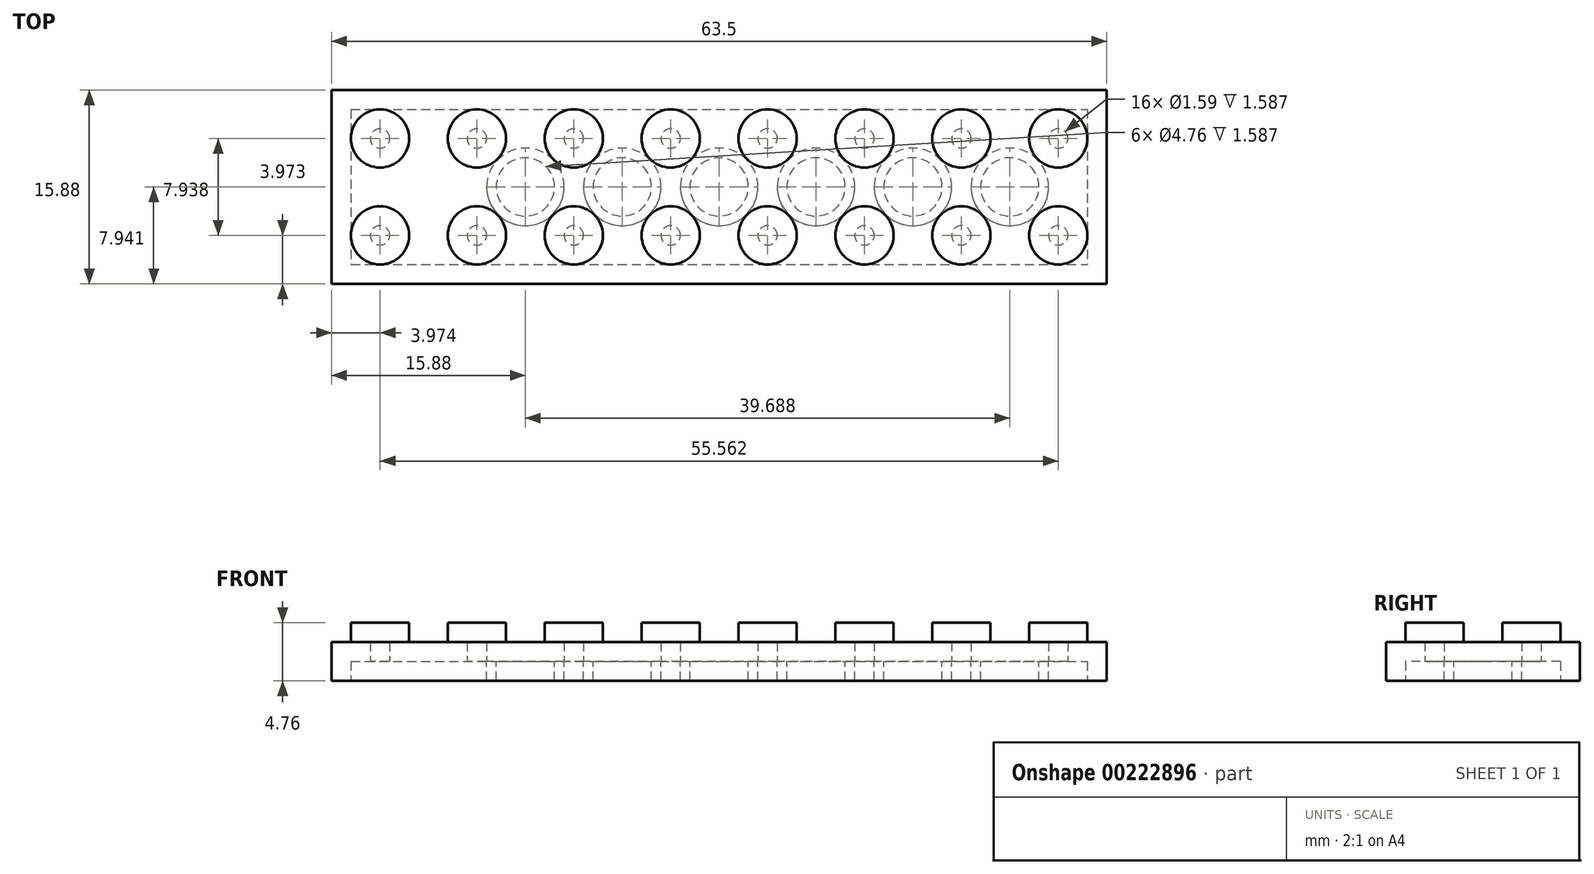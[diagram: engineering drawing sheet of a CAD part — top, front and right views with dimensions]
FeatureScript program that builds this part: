
annotation { "Feature Type Name" : "Feature", "Feature Type Description" : "" }
export const myFeature = defineFeature(function(context is Context, id is Id, definition is map)
    precondition{}
    {
        {
            var Q0;
            Q0=qCreatedBy(makeId("Top.planeOp"),FACE);
            var sketch = newSketch(context, id + "F0", { "sketchPlane" : qUnion([Q0])});
            skLineSegment(sketch, "E0.bottom", {"start": v(-15.88, 3.97) * mm, "end": v(47.62, 3.97) * mm});
            skLineSegment(sketch, "E0.top", {"start": v(-15.88, -11.9) * mm, "end": v(47.62, -11.9) * mm});
            skLineSegment(sketch, "E0.left", {"start": v(-15.88, 3.97) * mm, "end": v(-15.88, -11.9) * mm});
            skLineSegment(sketch, "E0.right", {"start": v(47.62, 3.97) * mm, "end": v(47.62, -11.9) * mm});
            skCircle(sketch, "E1", {"center": v(-11.9, 0) * mm, "radius": 2.38 * mm});
            skCircle(sketch, "E2.0.1.0", {"center": v(-11.9, -7.94) * mm, "radius": 2.38 * mm});
            skCircle(sketch, "E2.1.0.0", {"center": v(-3.97, 0) * mm, "radius": 2.38 * mm});
            skCircle(sketch, "E2.1.1.0", {"center": v(-3.97, -7.94) * mm, "radius": 2.38 * mm});
            skCircle(sketch, "E2.2.0.0", {"center": v(3.97, 0) * mm, "radius": 2.38 * mm});
            skCircle(sketch, "E2.2.1.0", {"center": v(3.97, -7.94) * mm, "radius": 2.38 * mm});
            skCircle(sketch, "E2.3.0.0", {"center": v(11.9, 0) * mm, "radius": 2.38 * mm});
            skCircle(sketch, "E2.3.1.0", {"center": v(11.9, -7.94) * mm, "radius": 2.38 * mm});
            skLineSegment(sketch, "E2.direction1", {"start": v(-11.9, 0) * mm, "end": v(-3.97, 0) * mm, "construction": true});
            skLineSegment(sketch, "E2.direction2", {"start": v(-11.9, 0) * mm, "end": v(-11.9, -7.94) * mm, "construction": true});
            skCircle(sketch, "E3.0.4.0", {"center": v(19.84, 0) * mm, "radius": 2.38 * mm});
            skCircle(sketch, "E3.0.4.1", {"center": v(19.84, -7.94) * mm, "radius": 2.38 * mm});
            skCircle(sketch, "E3.0.5.0", {"center": v(27.78, 0) * mm, "radius": 2.38 * mm});
            skCircle(sketch, "E3.0.5.1", {"center": v(27.78, -7.94) * mm, "radius": 2.38 * mm});
            skCircle(sketch, "E4.0.6.0", {"center": v(35.72, 0) * mm, "radius": 2.38 * mm});
            skCircle(sketch, "E4.0.6.1", {"center": v(35.72, -7.94) * mm, "radius": 2.38 * mm});
            skCircle(sketch, "E4.0.7.0", {"center": v(43.66, 0) * mm, "radius": 2.38 * mm});
            skCircle(sketch, "E4.0.7.1", {"center": v(43.66, -7.94) * mm, "radius": 2.38 * mm});
            skSolve(sketch);
        }
        {
            var Q0;
            Q0=makeQuery(id+"F0.imprint","IMPRINT",FACE,{"disambiguationData":[TD([[makeQuery(id+"F0.imprint","IMPRINT",EDGE,{"derivedFrom":sQuery(id+"F0.wireOp",EDGE,"E0.bottom")}),-1.0]])]});
            extrude(context, id + "F1", {"entities" : qUnion([Q0]), "depth" : 3.17 * mm});
        }
        {
            var Q0;
            Q0=makeQuery(id+"F0.imprint","IMPRINT",FACE,{"disambiguationData":[TD([[makeQuery(id+"F0.imprint","IMPRINT",EDGE,{"derivedFrom":sQuery(id+"F0.wireOp",EDGE,"E1")}),1.0]])]});
            var Q1;
            Q1=makeQuery(id+"F0.imprint","IMPRINT",FACE,{"disambiguationData":[TD([[makeQuery(id+"F0.imprint","IMPRINT",EDGE,{"derivedFrom":sQuery(id+"F0.wireOp",EDGE,"E2.0.1.0")}),1.0]])]});
            var Q2;
            Q2=makeQuery(id+"F0.imprint","IMPRINT",FACE,{"disambiguationData":[TD([[makeQuery(id+"F0.imprint","IMPRINT",EDGE,{"derivedFrom":sQuery(id+"F0.wireOp",EDGE,"E2.1.1.0")}),1.0]])]});
            var Q3;
            Q3=makeQuery(id+"F0.imprint","IMPRINT",FACE,{"disambiguationData":[TD([[makeQuery(id+"F0.imprint","IMPRINT",EDGE,{"derivedFrom":sQuery(id+"F0.wireOp",EDGE,"E2.1.0.0")}),1.0]])]});
            var Q4;
            Q4=makeQuery(id+"F0.imprint","IMPRINT",FACE,{"disambiguationData":[TD([[makeQuery(id+"F0.imprint","IMPRINT",EDGE,{"derivedFrom":sQuery(id+"F0.wireOp",EDGE,"E2.2.0.0")}),1.0]])]});
            var Q5;
            Q5=makeQuery(id+"F0.imprint","IMPRINT",FACE,{"disambiguationData":[TD([[makeQuery(id+"F0.imprint","IMPRINT",EDGE,{"derivedFrom":sQuery(id+"F0.wireOp",EDGE,"E2.2.1.0")}),1.0]])]});
            var Q6;
            Q6=makeQuery(id+"F0.imprint","IMPRINT",FACE,{"disambiguationData":[TD([[makeQuery(id+"F0.imprint","IMPRINT",EDGE,{"derivedFrom":sQuery(id+"F0.wireOp",EDGE,"E2.3.1.0")}),1.0]])]});
            var Q7;
            Q7=makeQuery(id+"F0.imprint","IMPRINT",FACE,{"disambiguationData":[TD([[makeQuery(id+"F0.imprint","IMPRINT",EDGE,{"derivedFrom":sQuery(id+"F0.wireOp",EDGE,"E2.3.0.0")}),1.0]])]});
            var Q8;
            Q8=makeQuery(id+"F0.imprint","IMPRINT",FACE,{"disambiguationData":[TD([[makeQuery(id+"F0.imprint","IMPRINT",EDGE,{"derivedFrom":sQuery(id+"F0.wireOp",EDGE,"E3.0.4.0")}),1.0]])]});
            var Q9;
            Q9=makeQuery(id+"F0.imprint","IMPRINT",FACE,{"disambiguationData":[TD([[makeQuery(id+"F0.imprint","IMPRINT",EDGE,{"derivedFrom":sQuery(id+"F0.wireOp",EDGE,"E3.0.5.0")}),1.0]])]});
            var Q10;
            Q10=makeQuery(id+"F0.imprint","IMPRINT",FACE,{"disambiguationData":[TD([[makeQuery(id+"F0.imprint","IMPRINT",EDGE,{"derivedFrom":sQuery(id+"F0.wireOp",EDGE,"E3.0.5.1")}),1.0]])]});
            var Q11;
            Q11=makeQuery(id+"F0.imprint","IMPRINT",FACE,{"disambiguationData":[TD([[makeQuery(id+"F0.imprint","IMPRINT",EDGE,{"derivedFrom":sQuery(id+"F0.wireOp",EDGE,"E3.0.4.1")}),1.0]])]});
            var Q12;
            Q12=makeQuery(id+"F0.imprint","IMPRINT",FACE,{"disambiguationData":[TD([[makeQuery(id+"F0.imprint","IMPRINT",EDGE,{"derivedFrom":sQuery(id+"F0.wireOp",EDGE,"E4.0.6.0")}),1.0]])]});
            var Q13;
            Q13=makeQuery(id+"F0.imprint","IMPRINT",FACE,{"disambiguationData":[TD([[makeQuery(id+"F0.imprint","IMPRINT",EDGE,{"derivedFrom":sQuery(id+"F0.wireOp",EDGE,"E4.0.7.0")}),1.0]])]});
            var Q14;
            Q14=makeQuery(id+"F0.imprint","IMPRINT",FACE,{"disambiguationData":[TD([[makeQuery(id+"F0.imprint","IMPRINT",EDGE,{"derivedFrom":sQuery(id+"F0.wireOp",EDGE,"E4.0.7.1")}),1.0]])]});
            var Q15;
            Q15=makeQuery(id+"F0.imprint","IMPRINT",FACE,{"disambiguationData":[TD([[makeQuery(id+"F0.imprint","IMPRINT",EDGE,{"derivedFrom":sQuery(id+"F0.wireOp",EDGE,"E4.0.6.1")}),1.0]])]});
            extrude(context, id + "F2", {"entities" : qUnion([Q0, Q1, Q2, Q3, Q4, Q5, Q6, Q7, Q8, Q9, Q10, Q11, Q12, Q13, Q14, Q15]), "operationType" : NewBodyOperationType.ADD, "depth" : 4.76 * mm});
        }
        {
            var Q0;
            {var subQ0=sQuery(id+"F0.wireOp",EDGE,"8b71ed98-f0e1-4300-85cb-82ad82c44b3e0.MirrorC");var subQ1=sQuery(id+"F0.wireOp",EDGE,"E1");Q0=makeQuery(id+"F2.boolean.opBoolean","MERGE",FACE,{"derivedFrom":[makeQuery(id+"F1.opExtrude","CAP_FACE",FACE,{"disambiguationData":[OSD([sQuery(id+"F0.wireOp",EDGE,"E0.bottom"),sQuery(id+"F0.wireOp",EDGE,"E0.top"),sQuery(id+"F0.wireOp",EDGE,"E0.left"),sQuery(id+"F0.wireOp",EDGE,"E0.right"),subQ1,subQ0])],"isStart":true}),makeQuery(id+"F2.opExtrude","CAP_FACE",FACE,{"disambiguationData":[OSD([subQ1])],"isStart":true}),makeQuery(id+"F2.opExtrude","CAP_FACE",FACE,{"disambiguationData":[OSD([subQ0])],"isStart":true})]});}
            shell(context, id + "F3", {"entities" : qUnion([Q0]), "thickness" : 1.59 * mm});
        }
        {
            var Q0;
            Q0=makeQuery(id+"F3.opShell","OFFSET_FACE",FACE,{"disambiguationData":[OSD([sQuery(id+"F0.wireOp",EDGE,"E0.bottom"),sQuery(id+"F0.wireOp",EDGE,"E0.top"),sQuery(id+"F0.wireOp",EDGE,"E0.left"),sQuery(id+"F0.wireOp",EDGE,"E0.right"),sQuery(id+"F0.wireOp",EDGE,"E1"),sQuery(id+"F0.wireOp",EDGE,"E2.0.1.0"),sQuery(id+"F0.wireOp",EDGE,"E2.1.0.0"),sQuery(id+"F0.wireOp",EDGE,"E2.1.1.0"),sQuery(id+"F0.wireOp",EDGE,"E2.2.0.0"),sQuery(id+"F0.wireOp",EDGE,"E2.2.1.0"),sQuery(id+"F0.wireOp",EDGE,"E2.3.0.0"),sQuery(id+"F0.wireOp",EDGE,"E2.3.1.0")])]});
            var sketch = newSketch(context, id + "F4", { "sketchPlane" : qUnion([Q0])});
            skLineSegment(sketch, "E5", {"start": v(-11.9, 7.94) * mm, "end": v(-3.97, 0) * mm});
            skCircle(sketch, "E6", {"center": v(-7.94, 3.97) * mm, "radius": 3.18 * mm});
            skCircle(sketch, "E7.0", {"center": v(-7.94, 3.97) * mm, "radius": 2.38 * mm});
            skCircle(sketch, "E8.1.0.0", {"center": v(0, 3.97) * mm, "radius": 3.18 * mm});
            skCircle(sketch, "E8.1.0.1", {"center": v(0, 3.97) * mm, "radius": 2.38 * mm});
            skCircle(sketch, "E8.2.0.0", {"center": v(7.94, 3.97) * mm, "radius": 3.18 * mm});
            skCircle(sketch, "E8.2.0.1", {"center": v(7.94, 3.97) * mm, "radius": 2.38 * mm});
            skLineSegment(sketch, "E8.direction1", {"start": v(-7.94, 3.97) * mm, "end": v(0, 3.97) * mm, "construction": true});
            skCircle(sketch, "E9.0.3.0", {"center": v(15.88, 3.97) * mm, "radius": 3.18 * mm});
            skCircle(sketch, "E9.2.3.0", {"center": v(15.88, 3.97) * mm, "radius": 2.38 * mm});
            skCircle(sketch, "E9.0.4.0", {"center": v(23.81, 3.97) * mm, "radius": 3.18 * mm});
            skCircle(sketch, "E9.2.4.0", {"center": v(23.81, 3.97) * mm, "radius": 2.38 * mm});
            skCircle(sketch, "E10.0.5.0", {"center": v(31.75, 3.97) * mm, "radius": 3.18 * mm});
            skCircle(sketch, "E10.2.5.0", {"center": v(31.75, 3.97) * mm, "radius": 2.38 * mm});
            skCircle(sketch, "E10.0.6.0", {"center": v(39.69, 3.97) * mm, "radius": 3.18 * mm});
            skCircle(sketch, "E10.2.6.0", {"center": v(39.69, 3.97) * mm, "radius": 2.38 * mm});
            skSolve(sketch);
        }
        {
            var Q0;
            {var subQ0=sQuery(id+"F4.wireOp",EDGE,"E6");var subQ1=sQuery(id+"F4.wireOp",EDGE,"E5");var subQ2=makeQuery(id+"F4.imprint","INTERSECT",VERTEX,{"disambiguationData":[OD(0.0)],"derivedFrom":[subQ1,subQ0]});Q0=makeQuery(id+"F4.imprint","IMPRINT",FACE,{"disambiguationData":[TD([[makeQuery(id+"F4.imprint","IMPRINT",EDGE,{"disambiguationData":[TD([[subQ2,-1.0]])],"derivedFrom":subQ1}),1.0]])]});}
            var Q1;
            {var subQ0=sQuery(id+"F4.wireOp",EDGE,"E6");var subQ1=sQuery(id+"F4.wireOp",EDGE,"E5");var subQ2=makeQuery(id+"F4.imprint","INTERSECT",VERTEX,{"disambiguationData":[OD(0.0)],"derivedFrom":[subQ1,subQ0]});Q1=makeQuery(id+"F4.imprint","IMPRINT",FACE,{"disambiguationData":[TD([[makeQuery(id+"F4.imprint","IMPRINT",EDGE,{"disambiguationData":[TD([[subQ2,-1.0]])],"derivedFrom":subQ1}),-1.0]])]});}
            var Q2;
            Q2=makeQuery(id+"F4.imprint","IMPRINT",FACE,{"disambiguationData":[TD([[makeQuery(id+"F4.imprint","IMPRINT",EDGE,{"derivedFrom":sQuery(id+"F4.wireOp",EDGE,"E8.1.0.0")}),1.0]])]});
            var Q3;
            Q3=makeQuery(id+"F4.imprint","IMPRINT",FACE,{"disambiguationData":[TD([[makeQuery(id+"F4.imprint","IMPRINT",EDGE,{"derivedFrom":sQuery(id+"F4.wireOp",EDGE,"E8.2.0.0")}),1.0]])]});
            var Q4;
            Q4=makeQuery(id+"F4.imprint","IMPRINT",FACE,{"disambiguationData":[TD([[makeQuery(id+"F4.imprint","IMPRINT",EDGE,{"derivedFrom":sQuery(id+"F4.wireOp",EDGE,"E9.0.3.0")}),1.0]])]});
            var Q5;
            Q5=makeQuery(id+"F4.imprint","IMPRINT",FACE,{"disambiguationData":[TD([[makeQuery(id+"F4.imprint","IMPRINT",EDGE,{"derivedFrom":sQuery(id+"F4.wireOp",EDGE,"E9.0.4.0")}),1.0]])]});
            var Q6;
            Q6=makeQuery(id+"F4.imprint","IMPRINT",FACE,{"disambiguationData":[TD([[makeQuery(id+"F4.imprint","IMPRINT",EDGE,{"derivedFrom":sQuery(id+"F4.wireOp",EDGE,"E10.0.5.0")}),1.0]])]});
            var Q7;
            Q7=makeQuery(id+"F4.imprint","IMPRINT",FACE,{"disambiguationData":[TD([[makeQuery(id+"F4.imprint","IMPRINT",EDGE,{"derivedFrom":sQuery(id+"F4.wireOp",EDGE,"E10.0.6.0")}),1.0]])]});
            extrude(context, id + "F5", {"entities" : qUnion([Q0, Q1, Q2, Q3, Q4, Q5, Q6, Q7]), "operationType" : NewBodyOperationType.ADD, "depth" : 1.59 * mm});
        }
    });
